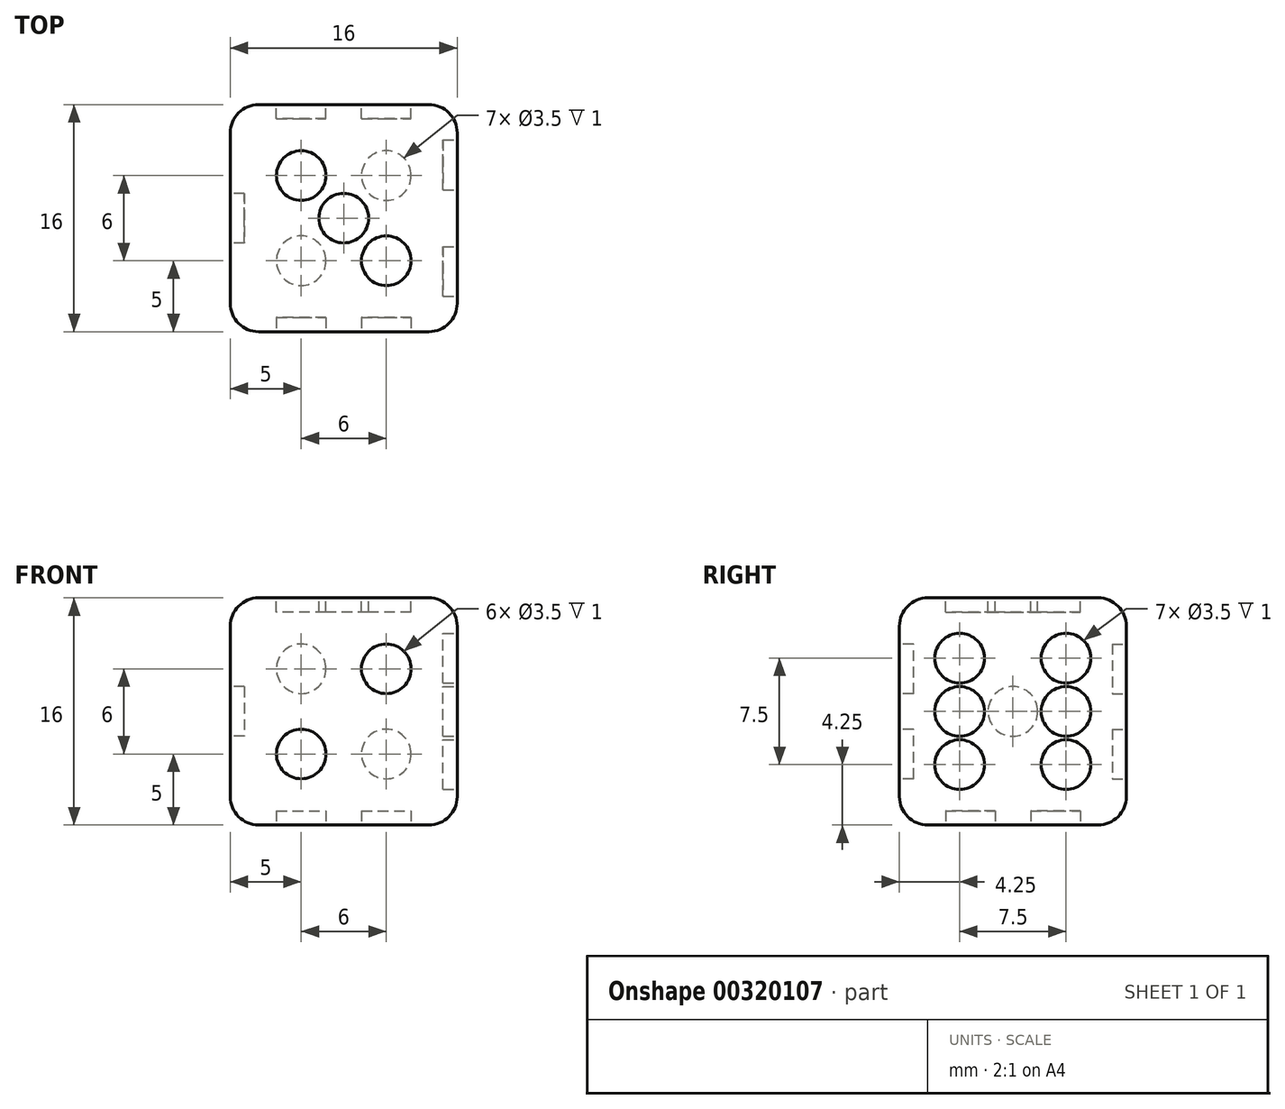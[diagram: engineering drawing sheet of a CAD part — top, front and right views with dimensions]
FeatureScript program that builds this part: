
annotation { "Feature Type Name" : "Feature", "Feature Type Description" : "" }
export const myFeature = defineFeature(function(context is Context, id is Id, definition is map)
    precondition{}
    {
        {
            var Q0;
            Q0=qCreatedBy(makeId("Front.planeOp"),FACE);
            var sketch = newSketch(context, id + "F0", { "sketchPlane" : qUnion([Q0])});
            skLineSegment(sketch, "E0.bottom", {"start": v(8, 8) * mm, "end": v(-8, 8) * mm});
            skLineSegment(sketch, "E0.top", {"start": v(8, -8) * mm, "end": v(-8, -8) * mm});
            skLineSegment(sketch, "E0.left", {"start": v(8, 8) * mm, "end": v(8, -8) * mm});
            skLineSegment(sketch, "E0.right", {"start": v(-8, 8) * mm, "end": v(-8, -8) * mm});
            skPoint(sketch, "E0.middle", {"position": v(0, 0) * mm});
            skSolve(sketch);
        }
        {
            var Q0;
            Q0=qSketchRegion(id+"F0",true);
            extrude(context, id + "F1", {"entities" : qUnion([Q0]), "depth" : 16 * mm});
        }
        {
            var Q0;
            Q0=makeQuery(id+"F1.opExtrude","CAP_EDGE",EDGE,{"disambiguationData":[OSD([sQuery(id+"F0.wireOp",EDGE,"E0.bottom")])],"isStart":false});
            var Q1;
            Q1=makeQuery(id+"F1.opExtrude","SWEPT_EDGE",EDGE,{"disambiguationData":[OSD([sQuery(id+"F0.wireOp",EDGE,"E0.bottom"),sQuery(id+"F0.wireOp",EDGE,"E0.right")])]});
            var Q2;
            Q2=makeQuery(id+"F1.opExtrude","SWEPT_EDGE",EDGE,{"disambiguationData":[OSD([sQuery(id+"F0.wireOp",EDGE,"E0.bottom"),sQuery(id+"F0.wireOp",EDGE,"E0.left")])]});
            var Q3;
            Q3=makeQuery(id+"F1.opExtrude","CAP_EDGE",EDGE,{"disambiguationData":[OSD([sQuery(id+"F0.wireOp",EDGE,"E0.bottom")])],"isStart":true});
            var Q4;
            Q4=makeQuery(id+"F1.opExtrude","CAP_EDGE",EDGE,{"disambiguationData":[OSD([sQuery(id+"F0.wireOp",EDGE,"E0.top")])],"isStart":true});
            var Q5;
            Q5=makeQuery(id+"F1.opExtrude","CAP_EDGE",EDGE,{"disambiguationData":[OSD([sQuery(id+"F0.wireOp",EDGE,"E0.left")])],"isStart":true});
            var Q6;
            Q6=makeQuery(id+"F1.opExtrude","SWEPT_EDGE",EDGE,{"disambiguationData":[OSD([sQuery(id+"F0.wireOp",EDGE,"E0.top"),sQuery(id+"F0.wireOp",EDGE,"E0.right")])]});
            var Q7;
            Q7=makeQuery(id+"F1.opExtrude","CAP_EDGE",EDGE,{"disambiguationData":[OSD([sQuery(id+"F0.wireOp",EDGE,"E0.right")])],"isStart":false});
            var Q8;
            Q8=makeQuery(id+"F1.opExtrude","CAP_EDGE",EDGE,{"disambiguationData":[OSD([sQuery(id+"F0.wireOp",EDGE,"E0.right")])],"isStart":true});
            var Q9;
            Q9=makeQuery(id+"F1.opExtrude","CAP_EDGE",EDGE,{"disambiguationData":[OSD([sQuery(id+"F0.wireOp",EDGE,"E0.top")])],"isStart":false});
            var Q10;
            Q10=makeQuery(id+"F1.opExtrude","CAP_EDGE",EDGE,{"disambiguationData":[OSD([sQuery(id+"F0.wireOp",EDGE,"E0.left")])],"isStart":false});
            var Q11;
            Q11=makeQuery(id+"F1.opExtrude","SWEPT_EDGE",EDGE,{"disambiguationData":[OSD([sQuery(id+"F0.wireOp",EDGE,"E0.top"),sQuery(id+"F0.wireOp",EDGE,"E0.left")])]});
            fillet(context, id + "F2", {"entities" : qUnion([Q0, Q1, Q2, Q3, Q4, Q5, Q6, Q7, Q8, Q9, Q10, Q11]), "radius" : 2 * mm, "tangentPropagation" : true, "allowEdgeOverflow" : false});
        }
        {
            var Q0;
            Q0=makeQuery(id+"F1.opExtrude","CAP_FACE",FACE,{"disambiguationData":[OSD([sQuery(id+"F0.wireOp",EDGE,"E0.bottom"),sQuery(id+"F0.wireOp",EDGE,"E0.top"),sQuery(id+"F0.wireOp",EDGE,"E0.left"),sQuery(id+"F0.wireOp",EDGE,"E0.right")])],"isStart":false});
            var sketch = newSketch(context, id + "F3", { "sketchPlane" : qUnion([Q0])});
            skLineSegment(sketch, "E1.bottom", {"start": v(3, 3) * mm, "end": v(-3, 3) * mm});
            skLineSegment(sketch, "E1.top", {"start": v(3, -3) * mm, "end": v(-3, -3) * mm});
            skLineSegment(sketch, "E1.left", {"start": v(3, 3) * mm, "end": v(3, -3) * mm});
            skLineSegment(sketch, "E1.right", {"start": v(-3, 3) * mm, "end": v(-3, -3) * mm});
            skPoint(sketch, "E1.middle", {"position": v(0, 0) * mm});
            skCircle(sketch, "E2", {"center": v(-3, -3) * mm, "radius": 1.75 * mm});
            skCircle(sketch, "E3", {"center": v(3, 3) * mm, "radius": 1.75 * mm});
            skSolve(sketch);
        }
        {
            var Q0;
            {var subQ0=sQuery(id+"F3.wireOp",EDGE,"E1.left");var subQ1=sQuery(id+"F3.wireOp",EDGE,"E1.bottom");var subQ2=makeQuery(id+"F3.imprint","INTERSECT",VERTEX,{"derivedFrom":[subQ1,subQ0]});Q0=makeQuery(id+"F3.imprint","IMPRINT",FACE,{"disambiguationData":[TD([[makeQuery(id+"F3.imprint","IMPRINT",EDGE,{"disambiguationData":[TD([[subQ2,-1.0]])],"derivedFrom":subQ1}),1.0]])]});}
            var Q1;
            {var subQ0=sQuery(id+"F3.wireOp",EDGE,"E1.right");var subQ1=sQuery(id+"F3.wireOp",EDGE,"E1.top");var subQ2=makeQuery(id+"F3.imprint","INTERSECT",VERTEX,{"derivedFrom":[subQ1,subQ0]});Q1=makeQuery(id+"F3.imprint","IMPRINT",FACE,{"disambiguationData":[TD([[makeQuery(id+"F3.imprint","IMPRINT",EDGE,{"disambiguationData":[TD([[subQ2,1.0]])],"derivedFrom":subQ1}),1.0]])]});}
            var Q2;
            {var subQ0=sQuery(id+"F3.wireOp",EDGE,"E1.right");var subQ1=sQuery(id+"F3.wireOp",EDGE,"E1.top");var subQ2=makeQuery(id+"F3.imprint","INTERSECT",VERTEX,{"derivedFrom":[subQ1,subQ0]});Q2=makeQuery(id+"F3.imprint","IMPRINT",FACE,{"disambiguationData":[TD([[makeQuery(id+"F3.imprint","IMPRINT",EDGE,{"disambiguationData":[TD([[subQ2,1.0]])],"derivedFrom":subQ1}),-1.0]])]});}
            var Q3;
            {var subQ0=sQuery(id+"F3.wireOp",EDGE,"E1.left");var subQ1=sQuery(id+"F3.wireOp",EDGE,"E1.bottom");var subQ2=makeQuery(id+"F3.imprint","INTERSECT",VERTEX,{"derivedFrom":[subQ1,subQ0]});Q3=makeQuery(id+"F3.imprint","IMPRINT",FACE,{"disambiguationData":[TD([[makeQuery(id+"F3.imprint","IMPRINT",EDGE,{"disambiguationData":[TD([[subQ2,-1.0]])],"derivedFrom":subQ1}),-1.0]])]});}
            extrude(context, id + "F4", {"entities" : qUnion([Q0, Q1, Q2, Q3]), "operationType" : NewBodyOperationType.REMOVE, "oppositeDirection" : true, "depth" : 1 * mm});
        }
        {
            var Q0;
            Q0=makeQuery(id+"F1.opExtrude","SWEPT_FACE",FACE,{"disambiguationData":[OSD([sQuery(id+"F0.wireOp",EDGE,"E0.bottom")])]});
            var sketch = newSketch(context, id + "F5", { "sketchPlane" : qUnion([Q0])});
            skLineSegment(sketch, "E4.bottom", {"start": v(3, -5) * mm, "end": v(-3, -5) * mm});
            skLineSegment(sketch, "E4.top", {"start": v(3, -11) * mm, "end": v(-3, -11) * mm});
            skLineSegment(sketch, "E4.left", {"start": v(3, -5) * mm, "end": v(3, -11) * mm});
            skLineSegment(sketch, "E4.right", {"start": v(-3, -5) * mm, "end": v(-3, -11) * mm});
            skPoint(sketch, "E4.middle", {"position": v(0, -8) * mm});
            skPoint(sketch, "E4.middle.positionSnap0", {"position": v(6, -8) * mm});
            skPoint(sketch, "E4.middle.positionSnap1", {"position": v(0, -14) * mm});
            skPoint(sketch, "E4.centerSnap0", {"position": v(6, -8) * mm});
            skPoint(sketch, "E4.centerSnap1", {"position": v(0, -14) * mm});
            skCircle(sketch, "E5", {"center": v(3, -11) * mm, "radius": 1.75 * mm});
            skCircle(sketch, "E6", {"center": v(0, -8) * mm, "radius": 1.75 * mm});
            skCircle(sketch, "E7", {"center": v(-3, -5) * mm, "radius": 1.75 * mm});
            skSolve(sketch);
        }
        {
            var Q0;
            {var subQ0=sQuery(id+"F5.wireOp",EDGE,"E4.right");var subQ1=sQuery(id+"F5.wireOp",EDGE,"E4.bottom");var subQ2=makeQuery(id+"F5.imprint","INTERSECT",VERTEX,{"derivedFrom":[subQ1,subQ0]});Q0=makeQuery(id+"F5.imprint","IMPRINT",FACE,{"disambiguationData":[TD([[makeQuery(id+"F5.imprint","IMPRINT",EDGE,{"disambiguationData":[TD([[subQ2,1.0]])],"derivedFrom":subQ1}),-1.0]])]});}
            var Q1;
            {var subQ0=sQuery(id+"F5.wireOp",EDGE,"E4.right");var subQ1=sQuery(id+"F5.wireOp",EDGE,"E4.bottom");var subQ2=makeQuery(id+"F5.imprint","INTERSECT",VERTEX,{"derivedFrom":[subQ1,subQ0]});Q1=makeQuery(id+"F5.imprint","IMPRINT",FACE,{"disambiguationData":[TD([[makeQuery(id+"F5.imprint","IMPRINT",EDGE,{"disambiguationData":[TD([[subQ2,1.0]])],"derivedFrom":subQ1}),1.0]])]});}
            var Q2;
            {var subQ0=sQuery(id+"F5.wireOp",EDGE,"E4.left");var subQ1=sQuery(id+"F5.wireOp",EDGE,"E4.top");var subQ2=makeQuery(id+"F5.imprint","INTERSECT",VERTEX,{"derivedFrom":[subQ1,subQ0]});Q2=makeQuery(id+"F5.imprint","IMPRINT",FACE,{"disambiguationData":[TD([[makeQuery(id+"F5.imprint","IMPRINT",EDGE,{"disambiguationData":[TD([[subQ2,-1.0]])],"derivedFrom":subQ1}),-1.0]])]});}
            var Q3;
            {var subQ0=sQuery(id+"F5.wireOp",EDGE,"E4.left");var subQ1=sQuery(id+"F5.wireOp",EDGE,"E4.top");var subQ2=makeQuery(id+"F5.imprint","INTERSECT",VERTEX,{"derivedFrom":[subQ1,subQ0]});Q3=makeQuery(id+"F5.imprint","IMPRINT",FACE,{"disambiguationData":[TD([[makeQuery(id+"F5.imprint","IMPRINT",EDGE,{"disambiguationData":[TD([[subQ2,-1.0]])],"derivedFrom":subQ1}),1.0]])]});}
            var Q4;
            Q4=makeQuery(id+"F5.imprint","IMPRINT",FACE,{"disambiguationData":[TD([[makeQuery(id+"F5.imprint","IMPRINT",EDGE,{"derivedFrom":sQuery(id+"F5.wireOp",EDGE,"E6")}),1.0]])]});
            extrude(context, id + "F6", {"entities" : qUnion([Q0, Q1, Q2, Q3, Q4]), "operationType" : NewBodyOperationType.REMOVE, "oppositeDirection" : true, "depth" : 1 * mm});
        }
        {
            var Q0;
            Q0=makeQuery(id+"F1.opExtrude","SWEPT_FACE",FACE,{"disambiguationData":[OSD([sQuery(id+"F0.wireOp",EDGE,"E0.left")])]});
            var sketch = newSketch(context, id + "F7", { "sketchPlane" : qUnion([Q0])});
            skLineSegment(sketch, "E8.bottom", {"start": v(-4.25, 3.75) * mm, "end": v(-11.75, 3.75) * mm});
            skLineSegment(sketch, "E8.top", {"start": v(-4.25, -3.75) * mm, "end": v(-11.75, -3.75) * mm});
            skLineSegment(sketch, "E8.left", {"start": v(-4.25, 3.75) * mm, "end": v(-4.25, -3.75) * mm});
            skLineSegment(sketch, "E8.right", {"start": v(-11.75, 3.75) * mm, "end": v(-11.75, -3.75) * mm});
            skPoint(sketch, "E8.middle", {"position": v(-8, 0) * mm});
            skPoint(sketch, "E8.middle.positionSnap0", {"position": v(-8, -6) * mm});
            skPoint(sketch, "E8.middle.positionSnap1", {"position": v(-14, 0) * mm});
            skPoint(sketch, "E8.centerSnap0", {"position": v(-8, -6) * mm});
            skPoint(sketch, "E8.centerSnap1", {"position": v(-14, 0) * mm});
            skCircle(sketch, "E9", {"center": v(-11.75, 3.75) * mm, "radius": 1.75 * mm});
            skCircle(sketch, "E10", {"center": v(-4.25, 3.75) * mm, "radius": 1.75 * mm});
            skCircle(sketch, "E11", {"center": v(-4.25, 0) * mm, "radius": 1.75 * mm});
            skCircle(sketch, "E12", {"center": v(-4.25, -3.75) * mm, "radius": 1.75 * mm});
            skCircle(sketch, "E13", {"center": v(-11.75, -3.75) * mm, "radius": 1.75 * mm});
            skCircle(sketch, "E14", {"center": v(-11.75, 0) * mm, "radius": 1.75 * mm});
            skSolve(sketch);
        }
        {
            var Q0;
            {var subQ0=sQuery(id+"F7.wireOp",EDGE,"E8.left");var subQ1=sQuery(id+"F7.wireOp",EDGE,"E8.bottom");var subQ2=makeQuery(id+"F7.imprint","INTERSECT",VERTEX,{"derivedFrom":[subQ1,subQ0]});Q0=makeQuery(id+"F7.imprint","IMPRINT",FACE,{"disambiguationData":[TD([[makeQuery(id+"F7.imprint","IMPRINT",EDGE,{"disambiguationData":[TD([[subQ2,-1.0]])],"derivedFrom":subQ1}),1.0]])]});}
            var Q1;
            {var subQ0=sQuery(id+"F7.wireOp",EDGE,"E8.left");var subQ1=sQuery(id+"F7.wireOp",EDGE,"E8.bottom");var subQ2=makeQuery(id+"F7.imprint","INTERSECT",VERTEX,{"derivedFrom":[subQ1,subQ0]});Q1=makeQuery(id+"F7.imprint","IMPRINT",FACE,{"disambiguationData":[TD([[makeQuery(id+"F7.imprint","IMPRINT",EDGE,{"disambiguationData":[TD([[subQ2,-1.0]])],"derivedFrom":subQ1}),-1.0]])]});}
            var Q2;
            {var subQ0=sQuery(id+"F7.wireOp",EDGE,"E8.right");var subQ1=sQuery(id+"F7.wireOp",EDGE,"E8.bottom");var subQ2=makeQuery(id+"F7.imprint","INTERSECT",VERTEX,{"derivedFrom":[subQ1,subQ0]});Q2=makeQuery(id+"F7.imprint","IMPRINT",FACE,{"disambiguationData":[TD([[makeQuery(id+"F7.imprint","IMPRINT",EDGE,{"disambiguationData":[TD([[subQ2,1.0]])],"derivedFrom":subQ1}),-1.0]])]});}
            var Q3;
            {var subQ0=sQuery(id+"F7.wireOp",EDGE,"E8.right");var subQ1=sQuery(id+"F7.wireOp",EDGE,"E8.bottom");var subQ2=makeQuery(id+"F7.imprint","INTERSECT",VERTEX,{"derivedFrom":[subQ1,subQ0]});Q3=makeQuery(id+"F7.imprint","IMPRINT",FACE,{"disambiguationData":[TD([[makeQuery(id+"F7.imprint","IMPRINT",EDGE,{"disambiguationData":[TD([[subQ2,1.0]])],"derivedFrom":subQ1}),1.0]])]});}
            var Q4;
            {var subQ0=sQuery(id+"F7.wireOp",EDGE,"E8.left");var subQ1=sQuery(id+"F7.wireOp",EDGE,"E8.top");var subQ2=makeQuery(id+"F7.imprint","INTERSECT",VERTEX,{"derivedFrom":[subQ1,subQ0]});Q4=makeQuery(id+"F7.imprint","IMPRINT",FACE,{"disambiguationData":[TD([[makeQuery(id+"F7.imprint","IMPRINT",EDGE,{"disambiguationData":[TD([[subQ2,-1.0]])],"derivedFrom":subQ1}),-1.0]])]});}
            var Q5;
            {var subQ0=sQuery(id+"F7.wireOp",EDGE,"E8.left");var subQ1=sQuery(id+"F7.wireOp",EDGE,"E8.top");var subQ2=makeQuery(id+"F7.imprint","INTERSECT",VERTEX,{"derivedFrom":[subQ1,subQ0]});Q5=makeQuery(id+"F7.imprint","IMPRINT",FACE,{"disambiguationData":[TD([[makeQuery(id+"F7.imprint","IMPRINT",EDGE,{"disambiguationData":[TD([[subQ2,-1.0]])],"derivedFrom":subQ1}),1.0]])]});}
            var Q6;
            {var subQ0=sQuery(id+"F7.wireOp",EDGE,"E8.right");var subQ1=sQuery(id+"F7.wireOp",EDGE,"E8.top");var subQ2=makeQuery(id+"F7.imprint","INTERSECT",VERTEX,{"derivedFrom":[subQ1,subQ0]});Q6=makeQuery(id+"F7.imprint","IMPRINT",FACE,{"disambiguationData":[TD([[makeQuery(id+"F7.imprint","IMPRINT",EDGE,{"disambiguationData":[TD([[subQ2,1.0]])],"derivedFrom":subQ1}),-1.0]])]});}
            var Q7;
            {var subQ0=sQuery(id+"F7.wireOp",EDGE,"E8.right");var subQ1=sQuery(id+"F7.wireOp",EDGE,"E8.top");var subQ2=makeQuery(id+"F7.imprint","INTERSECT",VERTEX,{"derivedFrom":[subQ1,subQ0]});Q7=makeQuery(id+"F7.imprint","IMPRINT",FACE,{"disambiguationData":[TD([[makeQuery(id+"F7.imprint","IMPRINT",EDGE,{"disambiguationData":[TD([[subQ2,1.0]])],"derivedFrom":subQ1}),1.0]])]});}
            var Q8;
            {var subQ0=sQuery(id+"F7.wireOp",EDGE,"E11");var subQ1=sQuery(id+"F7.wireOp",EDGE,"E8.left");var subQ2=makeQuery(id+"F7.imprint","INTERSECT",VERTEX,{"disambiguationData":[OD(0.0)],"derivedFrom":[subQ1,subQ0]});Q8=makeQuery(id+"F7.imprint","IMPRINT",FACE,{"disambiguationData":[TD([[makeQuery(id+"F7.imprint","IMPRINT",EDGE,{"disambiguationData":[TD([[subQ2,-1.0]])],"derivedFrom":subQ1}),-1.0]])]});}
            var Q9;
            {var subQ0=sQuery(id+"F7.wireOp",EDGE,"E11");var subQ1=sQuery(id+"F7.wireOp",EDGE,"E8.left");var subQ2=makeQuery(id+"F7.imprint","INTERSECT",VERTEX,{"disambiguationData":[OD(0.0)],"derivedFrom":[subQ1,subQ0]});Q9=makeQuery(id+"F7.imprint","IMPRINT",FACE,{"disambiguationData":[TD([[makeQuery(id+"F7.imprint","IMPRINT",EDGE,{"disambiguationData":[TD([[subQ2,-1.0]])],"derivedFrom":subQ1}),1.0]])]});}
            var Q10;
            {var subQ0=sQuery(id+"F7.wireOp",EDGE,"E14");var subQ1=sQuery(id+"F7.wireOp",EDGE,"E8.right");var subQ2=makeQuery(id+"F7.imprint","INTERSECT",VERTEX,{"disambiguationData":[OD(0.0)],"derivedFrom":[subQ1,subQ0]});Q10=makeQuery(id+"F7.imprint","IMPRINT",FACE,{"disambiguationData":[TD([[makeQuery(id+"F7.imprint","IMPRINT",EDGE,{"disambiguationData":[TD([[subQ2,-1.0]])],"derivedFrom":subQ1}),-1.0]])]});}
            var Q11;
            {var subQ0=sQuery(id+"F7.wireOp",EDGE,"E14");var subQ1=sQuery(id+"F7.wireOp",EDGE,"E8.right");var subQ2=makeQuery(id+"F7.imprint","INTERSECT",VERTEX,{"disambiguationData":[OD(0.0)],"derivedFrom":[subQ1,subQ0]});Q11=makeQuery(id+"F7.imprint","IMPRINT",FACE,{"disambiguationData":[TD([[makeQuery(id+"F7.imprint","IMPRINT",EDGE,{"disambiguationData":[TD([[subQ2,-1.0]])],"derivedFrom":subQ1}),1.0]])]});}
            extrude(context, id + "F8", {"entities" : qUnion([Q0, Q1, Q2, Q3, Q4, Q5, Q6, Q7, Q8, Q9, Q10, Q11]), "operationType" : NewBodyOperationType.REMOVE, "oppositeDirection" : true, "depth" : 1 * mm});
        }
        {
            var Q0;
            Q0=makeQuery(id+"F1.opExtrude","SWEPT_FACE",FACE,{"disambiguationData":[OSD([sQuery(id+"F0.wireOp",EDGE,"E0.top")])]});
            var sketch = newSketch(context, id + "F9", { "sketchPlane" : qUnion([Q0])});
            skLineSegment(sketch, "E15.bottom", {"start": v(3, 11) * mm, "end": v(-3, 11) * mm});
            skLineSegment(sketch, "E15.top", {"start": v(3, 5) * mm, "end": v(-3, 5) * mm});
            skLineSegment(sketch, "E15.left", {"start": v(3, 11) * mm, "end": v(3, 5) * mm});
            skLineSegment(sketch, "E15.right", {"start": v(-3, 11) * mm, "end": v(-3, 5) * mm});
            skPoint(sketch, "E15.middle", {"position": v(0, 8) * mm});
            skPoint(sketch, "E15.middle.positionSnap0", {"position": v(6, 8) * mm});
            skPoint(sketch, "E15.centerSnap0", {"position": v(6, 8) * mm});
            skCircle(sketch, "E16", {"center": v(-3, 11) * mm, "radius": 1.75 * mm});
            skCircle(sketch, "E17", {"center": v(3, 11) * mm, "radius": 1.75 * mm});
            skCircle(sketch, "E18", {"center": v(3, 5) * mm, "radius": 1.75 * mm});
            skCircle(sketch, "E19", {"center": v(-3, 5) * mm, "radius": 1.75 * mm});
            skSolve(sketch);
        }
        {
            var Q0;
            {var subQ0=sQuery(id+"F9.wireOp",EDGE,"E15.left");var subQ1=sQuery(id+"F9.wireOp",EDGE,"E15.bottom");var subQ2=makeQuery(id+"F9.imprint","INTERSECT",VERTEX,{"derivedFrom":[subQ1,subQ0]});Q0=makeQuery(id+"F9.imprint","IMPRINT",FACE,{"disambiguationData":[TD([[makeQuery(id+"F9.imprint","IMPRINT",EDGE,{"disambiguationData":[TD([[subQ2,-1.0]])],"derivedFrom":subQ1}),1.0]])]});}
            var Q1;
            {var subQ0=sQuery(id+"F9.wireOp",EDGE,"E15.left");var subQ1=sQuery(id+"F9.wireOp",EDGE,"E15.bottom");var subQ2=makeQuery(id+"F9.imprint","INTERSECT",VERTEX,{"derivedFrom":[subQ1,subQ0]});Q1=makeQuery(id+"F9.imprint","IMPRINT",FACE,{"disambiguationData":[TD([[makeQuery(id+"F9.imprint","IMPRINT",EDGE,{"disambiguationData":[TD([[subQ2,-1.0]])],"derivedFrom":subQ1}),-1.0]])]});}
            var Q2;
            {var subQ0=sQuery(id+"F9.wireOp",EDGE,"E15.right");var subQ1=sQuery(id+"F9.wireOp",EDGE,"E15.bottom");var subQ2=makeQuery(id+"F9.imprint","INTERSECT",VERTEX,{"derivedFrom":[subQ1,subQ0]});Q2=makeQuery(id+"F9.imprint","IMPRINT",FACE,{"disambiguationData":[TD([[makeQuery(id+"F9.imprint","IMPRINT",EDGE,{"disambiguationData":[TD([[subQ2,1.0]])],"derivedFrom":subQ1}),-1.0]])]});}
            var Q3;
            {var subQ0=sQuery(id+"F9.wireOp",EDGE,"E15.right");var subQ1=sQuery(id+"F9.wireOp",EDGE,"E15.bottom");var subQ2=makeQuery(id+"F9.imprint","INTERSECT",VERTEX,{"derivedFrom":[subQ1,subQ0]});Q3=makeQuery(id+"F9.imprint","IMPRINT",FACE,{"disambiguationData":[TD([[makeQuery(id+"F9.imprint","IMPRINT",EDGE,{"disambiguationData":[TD([[subQ2,1.0]])],"derivedFrom":subQ1}),1.0]])]});}
            var Q4;
            {var subQ0=sQuery(id+"F9.wireOp",EDGE,"E15.left");var subQ1=sQuery(id+"F9.wireOp",EDGE,"E15.top");var subQ2=makeQuery(id+"F9.imprint","INTERSECT",VERTEX,{"derivedFrom":[subQ1,subQ0]});Q4=makeQuery(id+"F9.imprint","IMPRINT",FACE,{"disambiguationData":[TD([[makeQuery(id+"F9.imprint","IMPRINT",EDGE,{"disambiguationData":[TD([[subQ2,-1.0]])],"derivedFrom":subQ1}),-1.0]])]});}
            var Q5;
            {var subQ0=sQuery(id+"F9.wireOp",EDGE,"E15.left");var subQ1=sQuery(id+"F9.wireOp",EDGE,"E15.top");var subQ2=makeQuery(id+"F9.imprint","INTERSECT",VERTEX,{"derivedFrom":[subQ1,subQ0]});Q5=makeQuery(id+"F9.imprint","IMPRINT",FACE,{"disambiguationData":[TD([[makeQuery(id+"F9.imprint","IMPRINT",EDGE,{"disambiguationData":[TD([[subQ2,-1.0]])],"derivedFrom":subQ1}),1.0]])]});}
            var Q6;
            {var subQ0=sQuery(id+"F9.wireOp",EDGE,"E15.right");var subQ1=sQuery(id+"F9.wireOp",EDGE,"E15.top");var subQ2=makeQuery(id+"F9.imprint","INTERSECT",VERTEX,{"derivedFrom":[subQ1,subQ0]});Q6=makeQuery(id+"F9.imprint","IMPRINT",FACE,{"disambiguationData":[TD([[makeQuery(id+"F9.imprint","IMPRINT",EDGE,{"disambiguationData":[TD([[subQ2,1.0]])],"derivedFrom":subQ1}),-1.0]])]});}
            var Q7;
            {var subQ0=sQuery(id+"F9.wireOp",EDGE,"E15.right");var subQ1=sQuery(id+"F9.wireOp",EDGE,"E15.top");var subQ2=makeQuery(id+"F9.imprint","INTERSECT",VERTEX,{"derivedFrom":[subQ1,subQ0]});Q7=makeQuery(id+"F9.imprint","IMPRINT",FACE,{"disambiguationData":[TD([[makeQuery(id+"F9.imprint","IMPRINT",EDGE,{"disambiguationData":[TD([[subQ2,1.0]])],"derivedFrom":subQ1}),1.0]])]});}
            extrude(context, id + "F10", {"entities" : qUnion([Q0, Q1, Q2, Q3, Q4, Q5, Q6, Q7]), "operationType" : NewBodyOperationType.REMOVE, "oppositeDirection" : true, "depth" : 1 * mm});
        }
        {
            var Q0;
            Q0=makeQuery(id+"F1.opExtrude","SWEPT_FACE",FACE,{"disambiguationData":[OSD([sQuery(id+"F0.wireOp",EDGE,"E0.right")])]});
            var sketch = newSketch(context, id + "F11", { "sketchPlane" : qUnion([Q0])});
            skCircle(sketch, "E20", {"center": v(8, 0) * mm, "radius": 1.75 * mm});
            skPoint(sketch, "E20.centerSnap0", {"position": v(8, -6) * mm});
            skSolve(sketch);
        }
        {
            var Q0;
            Q0=qSketchRegion(id+"F11",true);
            extrude(context, id + "F12", {"entities" : qUnion([Q0]), "operationType" : NewBodyOperationType.REMOVE, "oppositeDirection" : true, "depth" : 1 * mm});
        }
        {
            var Q0;
            Q0=makeQuery(id+"F1.opExtrude","CAP_FACE",FACE,{"disambiguationData":[OSD([sQuery(id+"F0.wireOp",EDGE,"E0.bottom"),sQuery(id+"F0.wireOp",EDGE,"E0.top"),sQuery(id+"F0.wireOp",EDGE,"E0.left"),sQuery(id+"F0.wireOp",EDGE,"E0.right")])],"isStart":true});
            var sketch = newSketch(context, id + "F13", { "sketchPlane" : qUnion([Q0])});
            skLineSegment(sketch, "E21.bottom", {"start": v(3, 3) * mm, "end": v(-3, 3) * mm});
            skLineSegment(sketch, "E21.top", {"start": v(3, -3) * mm, "end": v(-3, -3) * mm});
            skLineSegment(sketch, "E21.left", {"start": v(3, 3) * mm, "end": v(3, -3) * mm});
            skLineSegment(sketch, "E21.right", {"start": v(-3, 3) * mm, "end": v(-3, -3) * mm});
            skPoint(sketch, "E21.middle", {"position": v(0, 0) * mm});
            skCircle(sketch, "E22", {"center": v(-3, 3) * mm, "radius": 1.75 * mm});
            skCircle(sketch, "E23", {"center": v(-3, -3) * mm, "radius": 1.75 * mm});
            skCircle(sketch, "E24", {"center": v(0, 0) * mm, "radius": 1.75 * mm});
            skCircle(sketch, "E25", {"center": v(3, 3) * mm, "radius": 1.75 * mm});
            skCircle(sketch, "E26", {"center": v(3, -3) * mm, "radius": 1.75 * mm});
            skSolve(sketch);
        }
        {
            var Q0;
            {var subQ0=sQuery(id+"F13.wireOp",EDGE,"E21.left");var subQ1=sQuery(id+"F13.wireOp",EDGE,"E21.bottom");var subQ2=makeQuery(id+"F13.imprint","INTERSECT",VERTEX,{"derivedFrom":[subQ1,subQ0]});Q0=makeQuery(id+"F13.imprint","IMPRINT",FACE,{"disambiguationData":[TD([[makeQuery(id+"F13.imprint","IMPRINT",EDGE,{"disambiguationData":[TD([[subQ2,-1.0]])],"derivedFrom":subQ1}),1.0]])]});}
            var Q1;
            {var subQ0=sQuery(id+"F13.wireOp",EDGE,"E21.left");var subQ1=sQuery(id+"F13.wireOp",EDGE,"E21.bottom");var subQ2=makeQuery(id+"F13.imprint","INTERSECT",VERTEX,{"derivedFrom":[subQ1,subQ0]});Q1=makeQuery(id+"F13.imprint","IMPRINT",FACE,{"disambiguationData":[TD([[makeQuery(id+"F13.imprint","IMPRINT",EDGE,{"disambiguationData":[TD([[subQ2,-1.0]])],"derivedFrom":subQ1}),-1.0]])]});}
            var Q2;
            {var subQ0=sQuery(id+"F13.wireOp",EDGE,"E21.right");var subQ1=sQuery(id+"F13.wireOp",EDGE,"E21.bottom");var subQ2=makeQuery(id+"F13.imprint","INTERSECT",VERTEX,{"derivedFrom":[subQ1,subQ0]});Q2=makeQuery(id+"F13.imprint","IMPRINT",FACE,{"disambiguationData":[TD([[makeQuery(id+"F13.imprint","IMPRINT",EDGE,{"disambiguationData":[TD([[subQ2,1.0]])],"derivedFrom":subQ1}),-1.0]])]});}
            var Q3;
            {var subQ0=sQuery(id+"F13.wireOp",EDGE,"E21.right");var subQ1=sQuery(id+"F13.wireOp",EDGE,"E21.bottom");var subQ2=makeQuery(id+"F13.imprint","INTERSECT",VERTEX,{"derivedFrom":[subQ1,subQ0]});Q3=makeQuery(id+"F13.imprint","IMPRINT",FACE,{"disambiguationData":[TD([[makeQuery(id+"F13.imprint","IMPRINT",EDGE,{"disambiguationData":[TD([[subQ2,1.0]])],"derivedFrom":subQ1}),1.0]])]});}
            var Q4;
            {var subQ0=sQuery(id+"F13.wireOp",EDGE,"E21.left");var subQ1=sQuery(id+"F13.wireOp",EDGE,"E21.top");var subQ2=makeQuery(id+"F13.imprint","INTERSECT",VERTEX,{"derivedFrom":[subQ1,subQ0]});Q4=makeQuery(id+"F13.imprint","IMPRINT",FACE,{"disambiguationData":[TD([[makeQuery(id+"F13.imprint","IMPRINT",EDGE,{"disambiguationData":[TD([[subQ2,-1.0]])],"derivedFrom":subQ1}),-1.0]])]});}
            var Q5;
            {var subQ0=sQuery(id+"F13.wireOp",EDGE,"E21.left");var subQ1=sQuery(id+"F13.wireOp",EDGE,"E21.top");var subQ2=makeQuery(id+"F13.imprint","INTERSECT",VERTEX,{"derivedFrom":[subQ1,subQ0]});Q5=makeQuery(id+"F13.imprint","IMPRINT",FACE,{"disambiguationData":[TD([[makeQuery(id+"F13.imprint","IMPRINT",EDGE,{"disambiguationData":[TD([[subQ2,-1.0]])],"derivedFrom":subQ1}),1.0]])]});}
            var Q6;
            {var subQ0=sQuery(id+"F13.wireOp",EDGE,"E21.right");var subQ1=sQuery(id+"F13.wireOp",EDGE,"E21.top");var subQ2=makeQuery(id+"F13.imprint","INTERSECT",VERTEX,{"derivedFrom":[subQ1,subQ0]});Q6=makeQuery(id+"F13.imprint","IMPRINT",FACE,{"disambiguationData":[TD([[makeQuery(id+"F13.imprint","IMPRINT",EDGE,{"disambiguationData":[TD([[subQ2,1.0]])],"derivedFrom":subQ1}),-1.0]])]});}
            var Q7;
            {var subQ0=sQuery(id+"F13.wireOp",EDGE,"E21.right");var subQ1=sQuery(id+"F13.wireOp",EDGE,"E21.top");var subQ2=makeQuery(id+"F13.imprint","INTERSECT",VERTEX,{"derivedFrom":[subQ1,subQ0]});Q7=makeQuery(id+"F13.imprint","IMPRINT",FACE,{"disambiguationData":[TD([[makeQuery(id+"F13.imprint","IMPRINT",EDGE,{"disambiguationData":[TD([[subQ2,1.0]])],"derivedFrom":subQ1}),1.0]])]});}
            extrude(context, id + "F14", {"entities" : qUnion([Q0, Q1, Q2, Q3, Q4, Q5, Q6, Q7]), "operationType" : NewBodyOperationType.REMOVE, "oppositeDirection" : true, "depth" : 1 * mm});
        }
    });
